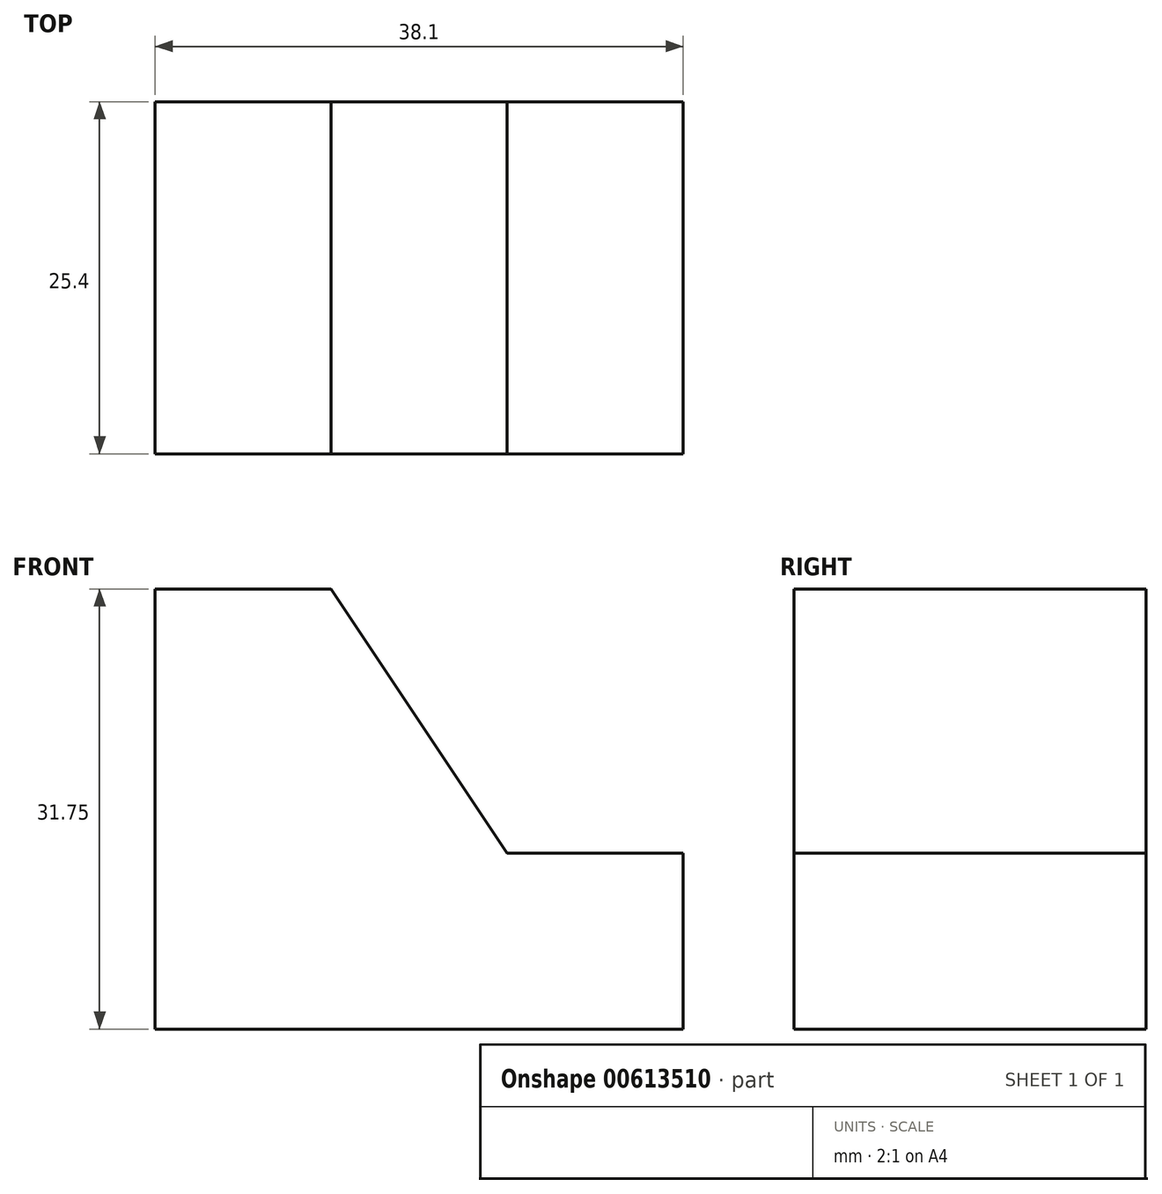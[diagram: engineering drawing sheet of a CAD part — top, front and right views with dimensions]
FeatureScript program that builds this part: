
annotation { "Feature Type Name" : "Feature", "Feature Type Description" : "" }
export const myFeature = defineFeature(function(context is Context, id is Id, definition is map)
    precondition{}
    {
        {
            var Q0;
            Q0=qCreatedBy(makeId("Front.planeOp"),FACE);
            var sketch = newSketch(context, id + "F0", { "sketchPlane" : qUnion([Q0])});
            skLineSegment(sketch, "E0", {"start": v(0, 0) * mm, "end": v(0, 31.75) * mm});
            skLineSegment(sketch, "E1", {"start": v(0, 31.75) * mm, "end": v(12.7, 31.75) * mm});
            skLineSegment(sketch, "E2", {"start": v(38.1, 12.7) * mm, "end": v(38.1, 0) * mm});
            skLineSegment(sketch, "E3", {"start": v(38.1, 0) * mm, "end": v(0, 0) * mm});
            skLineSegment(sketch, "E4", {"start": v(38.1, 12.7) * mm, "end": v(25.4, 12.7) * mm});
            skLineSegment(sketch, "E5", {"start": v(12.7, 31.75) * mm, "end": v(25.4, 12.7) * mm});
            skSolve(sketch);
        }
        {
            var Q0;
            Q0=makeQuery(id+"F0.imprint","IMPRINT",FACE,{"disambiguationData":[TD([[makeQuery(id+"F0.imprint","IMPRINT",EDGE,{"derivedFrom":sQuery(id+"F0.wireOp",EDGE,"E0")}),-1.0]])]});
            extrude(context, id + "F1", {"entities" : qUnion([Q0]), "depth" : 25.4 * mm, "offsetDistance" : 25.4 * mm});
        }
    });
